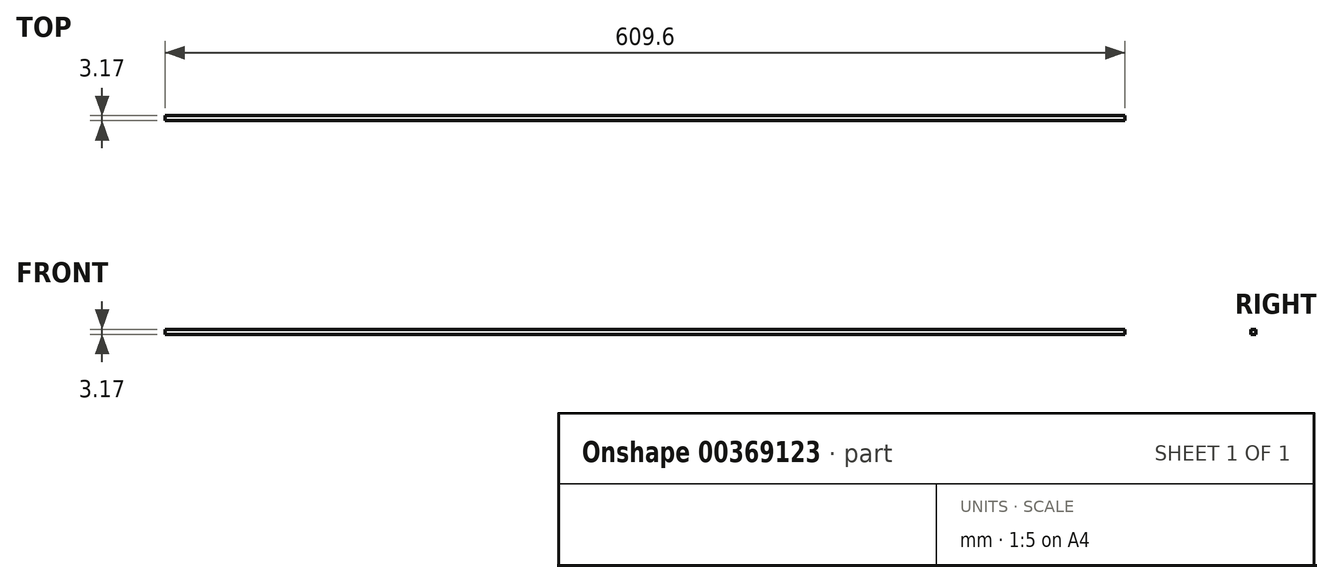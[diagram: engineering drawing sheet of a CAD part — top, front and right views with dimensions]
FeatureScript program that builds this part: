
annotation { "Feature Type Name" : "Feature", "Feature Type Description" : "" }
export const myFeature = defineFeature(function(context is Context, id is Id, definition is map)
    precondition{}
    {
        {
            var Q0;
            Q0=qCreatedBy(makeId("Front.planeOp"),FACE);
            var sketch = newSketch(context, id + "F0", { "sketchPlane" : qUnion([Q0])});
            skLineSegment(sketch, "E0.bottom", {"start": v(-300.02, -35.95) * mm, "end": v(309.58, -35.95) * mm});
            skLineSegment(sketch, "E0.top", {"start": v(-300.02, -39.12) * mm, "end": v(309.58, -39.12) * mm});
            skLineSegment(sketch, "E0.left", {"start": v(-300.02, -35.95) * mm, "end": v(-300.02, -39.12) * mm});
            skLineSegment(sketch, "E0.right", {"start": v(309.58, -35.95) * mm, "end": v(309.58, -39.12) * mm});
            skSolve(sketch);
        }
        {
            var Q0;
            Q0 = qSketchRegion(id + "F0", true);
            extrude(context, id + "F1", {"entities" : qUnion([Q0]), "depth" : 3.17 * mm});
        }
        {
            var Q0;
            Q0=makeQuery(id+"F1.opExtrude","SWEPT_BODY",BODY,{"disambiguationData":[OSD([sQuery(id+"F0.wireOp",EDGE,"E0.bottom"),sQuery(id+"F0.wireOp",EDGE,"E0.top"),sQuery(id+"F0.wireOp",EDGE,"E0.left"),sQuery(id+"F0.wireOp",EDGE,"E0.right")])]});
            transform(context, id + "F2", {"entities" : qUnion([Q0]), "transformType" : TransformType.TRANSLATION_3D, "dx" : 0 * mm, "dy" : 0 * mm, "dz" : 0 * mm, "makeCopy" : true});
        }
        {
            var Q0;
            Q0=makeQuery(id+"F1.opExtrude","SWEPT_BODY",BODY,{"disambiguationData":[OSD([sQuery(id+"F0.wireOp",EDGE,"E0.bottom"),sQuery(id+"F0.wireOp",EDGE,"E0.top"),sQuery(id+"F0.wireOp",EDGE,"E0.left"),sQuery(id+"F0.wireOp",EDGE,"E0.right")])]});
            transform(context, id + "F3", {"entities" : qUnion([Q0]), "transformType" : TransformType.TRANSLATION_3D, "dx" : 0 * mm, "dy" : 0 * mm, "dz" : 0 * mm, "makeCopy" : true});
        }
        {
            var Q0;
            Q0=makeQuery(id+"F3.opPattern","COPY",BODY,{"derivedFrom":makeQuery(id+"F1.opExtrude","SWEPT_BODY",BODY,{"disambiguationData":[OSD([sQuery(id+"F0.wireOp",EDGE,"E0.bottom"),sQuery(id+"F0.wireOp",EDGE,"E0.top"),sQuery(id+"F0.wireOp",EDGE,"E0.left"),sQuery(id+"F0.wireOp",EDGE,"E0.right")])]}),"instanceName":"1"});
            var Q1;
            Q1=makeQuery(id+"F1.opExtrude","SWEPT_BODY",BODY,{"disambiguationData":[OSD([sQuery(id+"F0.wireOp",EDGE,"E0.bottom"),sQuery(id+"F0.wireOp",EDGE,"E0.top"),sQuery(id+"F0.wireOp",EDGE,"E0.left"),sQuery(id+"F0.wireOp",EDGE,"E0.right")])]});
            transform(context, id + "F4", {"entities" : qUnion([Q0, Q1]), "transformType" : TransformType.TRANSLATION_3D, "dx" : 0 * mm, "dy" : 0 * mm, "dz" : 0 * mm, "makeCopy" : true});
        }
    });
